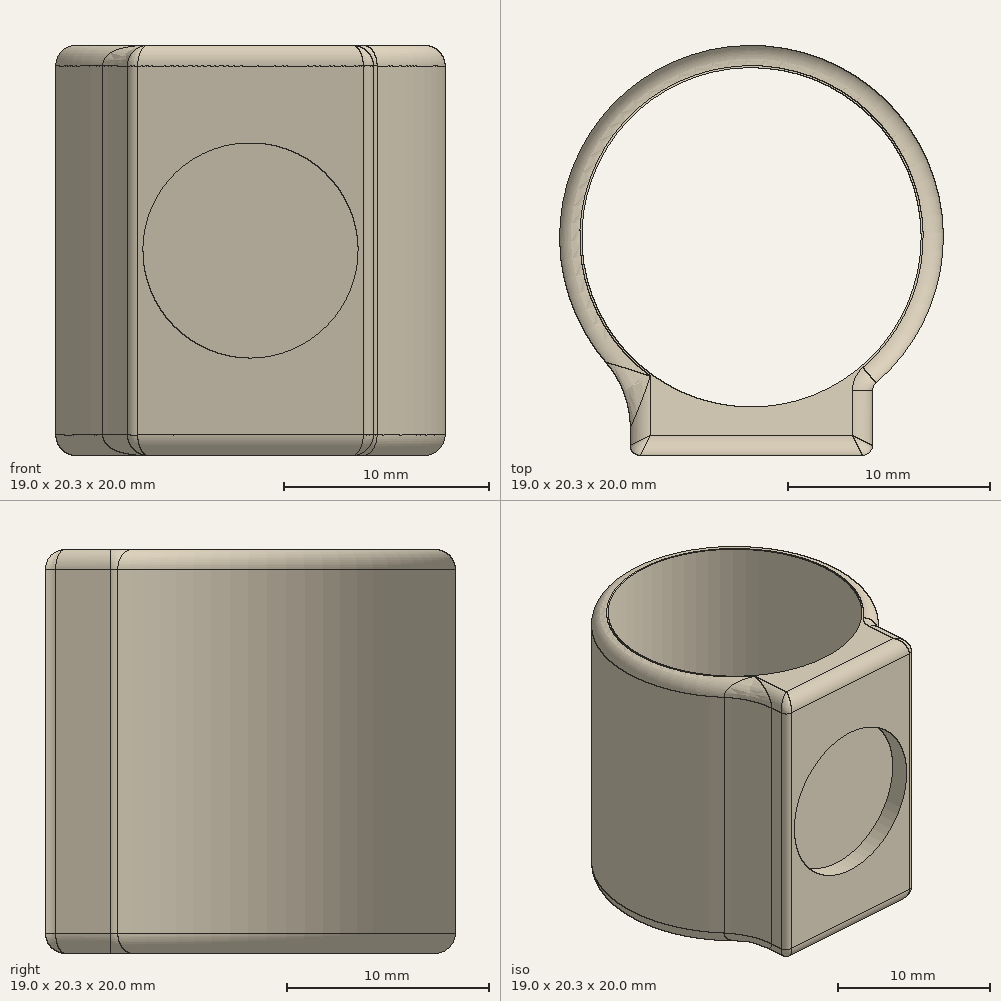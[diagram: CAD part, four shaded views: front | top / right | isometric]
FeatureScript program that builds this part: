
annotation { "Feature Type Name" : "Feature", "Feature Type Description" : "" }
export const myFeature = defineFeature(function(context is Context, id is Id, definition is map)
    precondition{}
    {
        {
            var Q0;
            Q0=qCreatedBy(makeId("Top.planeOp"),FACE);
            var sketch = newSketch(context, id + "F0", { "sketchPlane" : qUnion([Q0])});
            skCircle(sketch, "E0", {"center": v(0, 0) * mm, "radius": 8.4 * mm});
            skCircle(sketch, "E1", {"center": v(0, 0) * mm, "radius": 9.5 * mm});
            skLineSegment(sketch, "E2", {"start": v(0, -9.5) * mm, "end": v(0, -10.8) * mm});
            skLineSegment(sketch, "E3", {"start": v(0, -10.8) * mm, "end": v(6, -10.8) * mm});
            skLineSegment(sketch, "E4", {"start": v(6, -10.8) * mm, "end": v(-6, -10.8) * mm});
            skLineSegment(sketch, "E5", {"start": v(-6, -10.8) * mm, "end": v(-6, -7.37) * mm});
            skLineSegment(sketch, "E6", {"start": v(6, -10.8) * mm, "end": v(6, -7.37) * mm});
            skSolve(sketch);
        }
        {
            var Q0;
            {var subQ0=sQuery(id+"F0.wireOp",EDGE,"E2");Q0=makeQuery(id+"F0.imprint","IMPRINT",FACE,{"disambiguationData":[TD([[makeQuery(id+"F0.imprint","IMPRINT",EDGE,{"derivedFrom":subQ0}),-1.0]])]});}
            var Q1;
            {var subQ0=sQuery(id+"F0.wireOp",EDGE,"E2");Q1=makeQuery(id+"F0.imprint","IMPRINT",FACE,{"disambiguationData":[TD([[makeQuery(id+"F0.imprint","IMPRINT",EDGE,{"derivedFrom":subQ0}),1.0]])]});}
            var Q2;
            Q2=makeQuery(id+"F0.imprint","IMPRINT",FACE,{"disambiguationData":[TD([[makeQuery(id+"F0.imprint","IMPRINT",EDGE,{"derivedFrom":sQuery(id+"F0.wireOp",EDGE,"E0")}),-1.0]])]});
            extrude(context, id + "F1", {"entities" : qUnion([Q0, Q1, Q2]), "endBound" : BoundingType.SYMMETRIC, "depth" : 20 * mm, "offsetDistance" : 25 * mm});
        }
        {
            var Q0;
            Q0=makeQuery(id+"F1.opExtrude","SWEPT_EDGE",EDGE,{"disambiguationData":[OSD([sQuery(id+"F0.wireOp",EDGE,"E4"),sQuery(id+"F0.wireOp",EDGE,"E5")])]});
            var Q1;
            Q1=makeQuery(id+"F1.opExtrude","SWEPT_EDGE",EDGE,{"disambiguationData":[OSD([sQuery(id+"F0.wireOp",EDGE,"E4"),sQuery(id+"F0.wireOp",EDGE,"E6")])]});
            fillet(context, id + "F2", {"entities" : qUnion([Q0, Q1]), "radius" : 0.5 * mm, "tangentPropagation" : true, "allowEdgeOverflow" : false});
        }
        {
            var Q0;
            Q0=makeQuery(id+"F1.opExtrude","SWEPT_FACE",FACE,{"disambiguationData":[OSD([sQuery(id+"F0.wireOp",EDGE,"E4")])]});
            var sketch = newSketch(context, id + "F3", { "sketchPlane" : qUnion([Q0])});
            skCircle(sketch, "E7", {"center": v(0, 0) * mm, "radius": 5.25 * mm});
            skSolve(sketch);
        }
        {
            var Q0;
            Q0=makeQuery(id+"F3.imprint","IMPRINT",FACE,{"disambiguationData":[TD([[makeQuery(id+"F3.imprint","IMPRINT",EDGE,{"derivedFrom":sQuery(id+"F3.wireOp",EDGE,"E7")}),1.0]])]});
            extrude(context, id + "F4", {"entities" : qUnion([Q0]), "operationType" : NewBodyOperationType.REMOVE, "oppositeDirection" : true, "depth" : 1.3 * mm, "offsetDistance" : 25 * mm});
        }
        {
            var Q0;
            Q0=makeQuery(id+"F1.opExtrude","CAP_EDGE",EDGE,{"disambiguationData":[OSD([sQuery(id+"F0.wireOp",EDGE,"E1")])],"isStart":false});
            var Q1;
            Q1=makeQuery(id+"F1.opExtrude","CAP_EDGE",EDGE,{"disambiguationData":[OSD([sQuery(id+"F0.wireOp",EDGE,"E4")])],"isStart":false});
            var Q2;
            Q2=makeQuery(id+"F1.opExtrude","CAP_EDGE",EDGE,{"disambiguationData":[OSD([sQuery(id+"F0.wireOp",EDGE,"E6")])],"isStart":true});
            var Q3;
            Q3=makeQuery(id+"F1.opExtrude","CAP_EDGE",EDGE,{"disambiguationData":[OSD([sQuery(id+"F0.wireOp",EDGE,"E1")])],"isStart":true});
            fillet(context, id + "F5", {"entities" : qUnion([Q0, Q1, Q2, Q3]), "radius" : 1 * mm, "tangentPropagation" : true, "allowEdgeOverflow" : false});
        }
        {
            var Q0;
            Q0=makeQuery(id+"F1.opExtrude","SWEPT_EDGE",EDGE,{"disambiguationData":[OSD([sQuery(id+"F0.wireOp",EDGE,"E1"),sQuery(id+"F0.wireOp",EDGE,"E6")])]});
            var Q1;
            Q1=makeQuery(id+"F1.opExtrude","SWEPT_EDGE",EDGE,{"disambiguationData":[OSD([sQuery(id+"F0.wireOp",EDGE,"E1"),sQuery(id+"F0.wireOp",EDGE,"E5")])]});
            fillet(context, id + "F6", {"entities" : qUnion([Q0, Q1]), "radius" : 5 * mm, "tangentPropagation" : true, "allowEdgeOverflow" : false});
        }
    });
